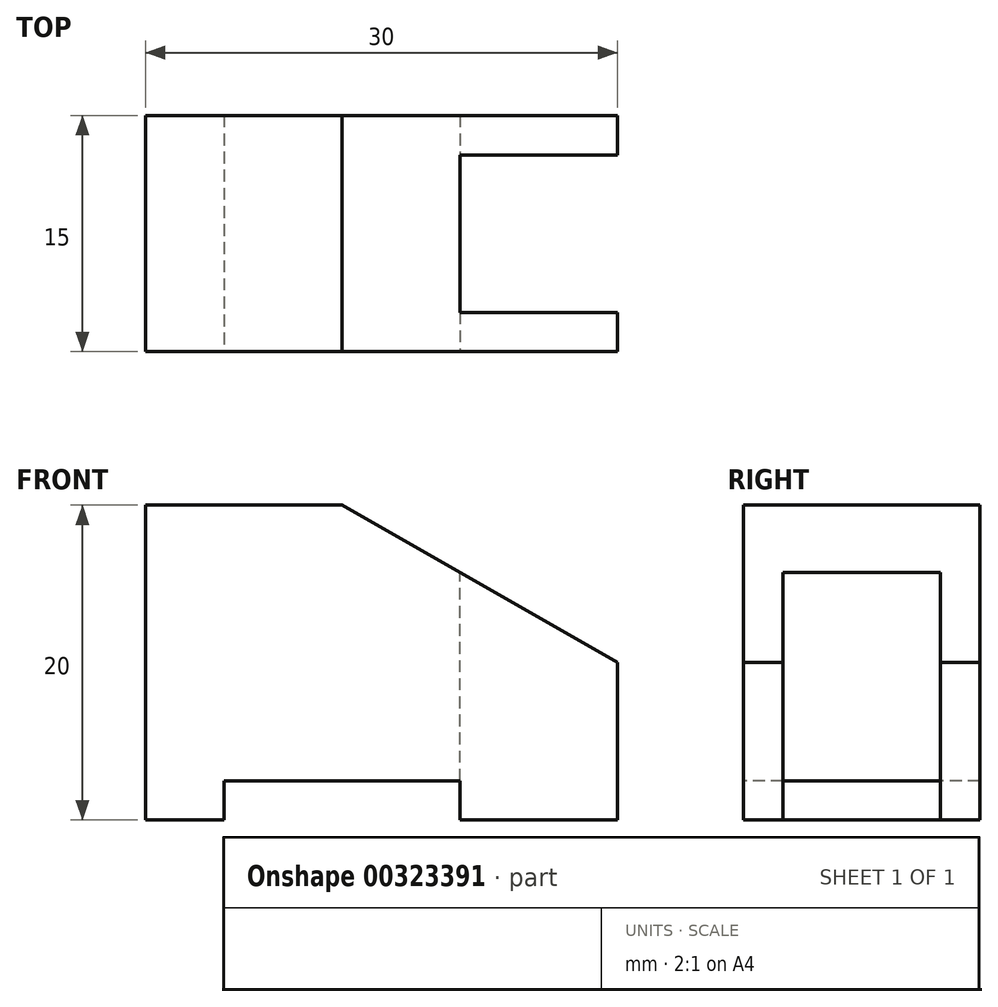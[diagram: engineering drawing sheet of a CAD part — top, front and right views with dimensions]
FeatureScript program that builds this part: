
annotation { "Feature Type Name" : "Feature", "Feature Type Description" : "" }
export const myFeature = defineFeature(function(context is Context, id is Id, definition is map)
    precondition{}
    {
        {
            var Q0;
            Q0=qCreatedBy(makeId("Front.planeOp"),FACE);
            var sketch = newSketch(context, id + "F0", { "sketchPlane" : qUnion([Q0])});
            skLineSegment(sketch, "E0", {"start": v(0, 0) * mm, "end": v(0, -20) * mm});
            skLineSegment(sketch, "E1", {"start": v(0, -20) * mm, "end": v(5, -20) * mm});
            skLineSegment(sketch, "E2", {"start": v(5, -20) * mm, "end": v(5, -17.5) * mm});
            skLineSegment(sketch, "E3", {"start": v(5, -17.5) * mm, "end": v(20, -17.5) * mm});
            skLineSegment(sketch, "E4", {"start": v(20, -17.5) * mm, "end": v(20, -20) * mm});
            skLineSegment(sketch, "E5", {"start": v(20, -20) * mm, "end": v(30, -20) * mm});
            skLineSegment(sketch, "E6", {"start": v(30, -20) * mm, "end": v(30, -10) * mm});
            skLineSegment(sketch, "E7", {"start": v(30, -10) * mm, "end": v(12.5, 0) * mm});
            skLineSegment(sketch, "E8", {"start": v(12.5, 0) * mm, "end": v(0, 0) * mm});
            skSolve(sketch);
        }
        {
            var Q0;
            Q0 = qSketchRegion(id + "F0", true);
            extrude(context, id + "F1", {"entities" : qUnion([Q0]), "oppositeDirection" : true, "depth" : 15 * mm});
        }
        {
            var Q0;
            Q0=makeQuery(id+"F1.opExtrude","SWEPT_FACE",FACE,{"disambiguationData":[OSD([sQuery(id+"F0.wireOp",EDGE,"E8")])]});
            var sketch = newSketch(context, id + "F2", { "sketchPlane" : qUnion([Q0])});
            skLineSegment(sketch, "E9.0.0", {"start": v(12.5, 0) * mm, "end": v(30, 0) * mm});
            skLineSegment(sketch, "E9.0.1", {"start": v(30, 0) * mm, "end": v(30, 15) * mm});
            skLineSegment(sketch, "E9.0.2", {"start": v(30, 15) * mm, "end": v(12.5, 15) * mm});
            skLineSegment(sketch, "E9.0.3", {"start": v(12.5, 15) * mm, "end": v(12.5, 0) * mm});
            skLineSegment(sketch, "E10", {"start": v(30, 12.5) * mm, "end": v(20, 12.5) * mm});
            skLineSegment(sketch, "E11", {"start": v(20, 12.5) * mm, "end": v(20, 2.5) * mm});
            skLineSegment(sketch, "E12", {"start": v(20, 2.5) * mm, "end": v(30, 2.5) * mm});
            skLineSegment(sketch, "E13", {"start": v(30, 2.5) * mm, "end": v(30, 12.5) * mm});
            skSolve(sketch);
        }
        {
            var Q0;
            Q0=makeQuery(id+"F2.imprint","IMPRINT",FACE,{"disambiguationData":[TD([[makeQuery(id+"F2.imprint","IMPRINT",EDGE,{"derivedFrom":sQuery(id+"F2.wireOp",EDGE,"E10")}),1.0]])]});
            extrude(context, id + "F3", {"entities" : qUnion([Q0]), "operationType" : NewBodyOperationType.REMOVE, "oppositeDirection" : true, "depth" : 25 * mm});
        }
    });
